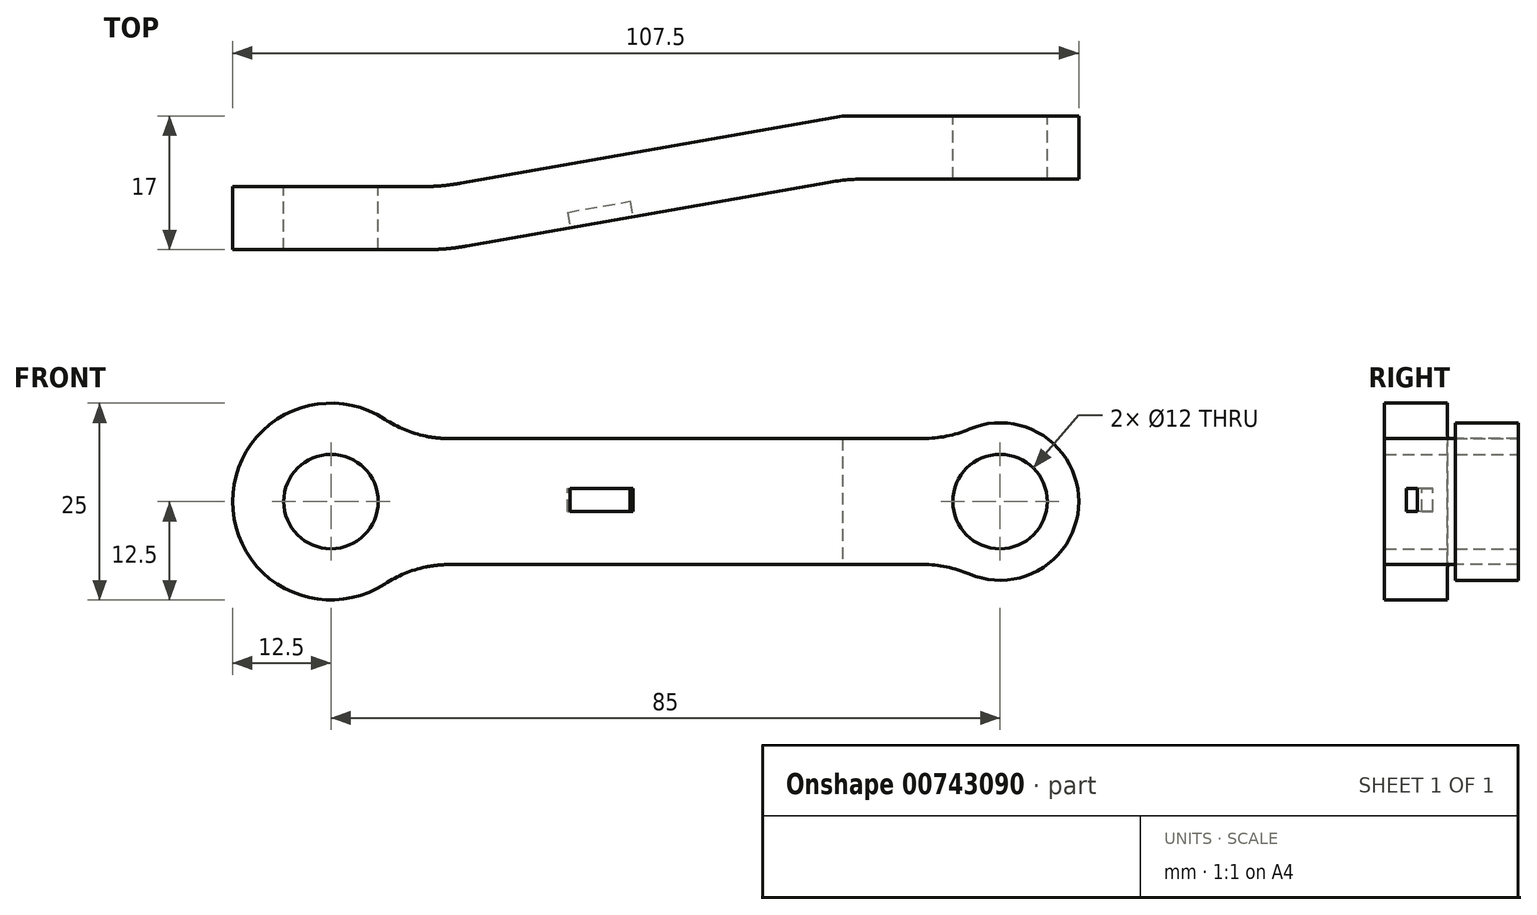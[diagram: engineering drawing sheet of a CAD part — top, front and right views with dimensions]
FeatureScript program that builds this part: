
annotation { "Feature Type Name" : "Feature", "Feature Type Description" : "" }
export const myFeature = defineFeature(function(context is Context, id is Id, definition is map)
    precondition{}
    {
        {
            var Q0;
            Q0=qCreatedBy(makeId("Front.planeOp"),FACE);
            var sketch = newSketch(context, id + "F0", { "sketchPlane" : qUnion([Q0])});
            skCircle(sketch, "E0", {"center": v(0, 0) * mm, "radius": 10 * mm});
            skCircle(sketch, "E1", {"center": v(-85, 0) * mm, "radius": 12.5 * mm});
            skCircle(sketch, "E2", {"center": v(-85, 0) * mm, "radius": 6 * mm});
            skCircle(sketch, "E3", {"center": v(0, 0) * mm, "radius": 6 * mm});
            skLineSegment(sketch, "E4", {"start": v(-85, 0) * mm, "end": v(0, 0) * mm, "construction": true});
            skLineSegment(sketch, "E5", {"start": v(-75.4, 8) * mm, "end": v(-6, 8) * mm});
            skLineSegment(sketch, "E6", {"start": v(-75.4, -8) * mm, "end": v(-6, -8) * mm});
            skSolve(sketch);
        }
        {
            var Q0;
            Q0=makeQuery(id+"F0.imprint","IMPRINT",FACE,{"disambiguationData":[TD([[makeQuery(id+"F0.imprint","IMPRINT",EDGE,{"derivedFrom":sQuery(id+"F0.wireOp",EDGE,"E2")}),-1.0]])]});
            var Q1;
            {var subQ0=sQuery(id+"F0.wireOp",EDGE,"E5");Q1=makeQuery(id+"F0.imprint","IMPRINT",FACE,{"disambiguationData":[TD([[makeQuery(id+"F0.imprint","IMPRINT",EDGE,{"derivedFrom":subQ0}),-1.0]])]});}
            var Q2;
            Q2=makeQuery(id+"F0.imprint","IMPRINT",FACE,{"disambiguationData":[TD([[makeQuery(id+"F0.imprint","IMPRINT",EDGE,{"derivedFrom":sQuery(id+"F0.wireOp",EDGE,"E3")}),-1.0]])]});
            extrude(context, id + "F1", {"entities" : qUnion([Q0, Q1, Q2]), "depth" : 25 * mm});
        }
        {
            var Q0;
            Q0=qCreatedBy(makeId("Top.planeOp"),FACE);
            var sketch = newSketch(context, id + "F2", { "sketchPlane" : qUnion([Q0])});
            skLineSegment(sketch, "E7", {"start": v(-110.22, -9) * mm, "end": v(-71.04, -9) * mm});
            skLineSegment(sketch, "E8", {"start": v(-71.04, -9) * mm, "end": v(-20, 0) * mm});
            skLineSegment(sketch, "E9", {"start": v(-20, 0) * mm, "end": v(29.22, 0) * mm});
            skLineSegment(sketch, "E10", {"start": v(29.22, 0) * mm, "end": v(29.22, -8) * mm});
            skLineSegment(sketch, "E11", {"start": v(29.22, -8) * mm, "end": v(-19.3, -8) * mm});
            skLineSegment(sketch, "E12", {"start": v(-19.3, -8) * mm, "end": v(-70.34, -17) * mm});
            skLineSegment(sketch, "E13", {"start": v(-70.34, -17) * mm, "end": v(-110.22, -17) * mm});
            skLineSegment(sketch, "E14", {"start": v(-110.22, -17) * mm, "end": v(-110.22, -9) * mm});
            skSolve(sketch);
        }
        {
            var Q0;
            Q0=makeQuery(id+"F2.imprint","IMPRINT",FACE,{"disambiguationData":[TD([[makeQuery(id+"F2.imprint","IMPRINT",EDGE,{"derivedFrom":sQuery(id+"F2.wireOp",EDGE,"E7")}),-1.0]])]});
            extrude(context, id + "F3", {"entities" : qUnion([Q0]), "operationType" : NewBodyOperationType.INTERSECT, "endBound" : BoundingType.SYMMETRIC, "depth" : 40 * mm});
        }
        {
            var Q0;
            Q0=makeQuery(id+"F3.boolean.opBoolean","COPY",EDGE,{"derivedFrom":makeQuery(id+"F3.opExtrude","SWEPT_EDGE",EDGE,{"disambiguationData":[OSD([sQuery(id+"F2.wireOp",EDGE,"E12"),sQuery(id+"F2.wireOp",EDGE,"E13")])]})});
            var Q1;
            Q1=makeQuery(id+"F3.boolean.opBoolean","COPY",EDGE,{"derivedFrom":makeQuery(id+"F3.opExtrude","SWEPT_EDGE",EDGE,{"disambiguationData":[OSD([sQuery(id+"F2.wireOp",EDGE,"E11"),sQuery(id+"F2.wireOp",EDGE,"E12")])]})});
            var Q2;
            Q2=makeQuery(id+"F3.boolean.opBoolean","COPY",EDGE,{"derivedFrom":makeQuery(id+"F3.opExtrude","SWEPT_EDGE",EDGE,{"disambiguationData":[OSD([sQuery(id+"F2.wireOp",EDGE,"E8"),sQuery(id+"F2.wireOp",EDGE,"E9")])]})});
            var Q3;
            Q3=makeQuery(id+"F3.boolean.opBoolean","COPY",EDGE,{"derivedFrom":makeQuery(id+"F3.opExtrude","SWEPT_EDGE",EDGE,{"disambiguationData":[OSD([sQuery(id+"F2.wireOp",EDGE,"E7"),sQuery(id+"F2.wireOp",EDGE,"E8")])]})});
            fillet(context, id + "F4", {"entities" : qUnion([Q0, Q1, Q2, Q3]), "radius" : 30 * mm, "tangentPropagation" : true, "allowEdgeOverflow" : false});
        }
        {
            var Q0;
            Q0=makeQuery(id+"F1.opExtrude","SWEPT_EDGE",EDGE,{"disambiguationData":[OSD([sQuery(id+"F0.wireOp",EDGE,"E1"),sQuery(id+"F0.wireOp",EDGE,"E5")])]});
            var Q1;
            Q1=makeQuery(id+"F1.opExtrude","SWEPT_EDGE",EDGE,{"disambiguationData":[OSD([sQuery(id+"F0.wireOp",EDGE,"E0"),sQuery(id+"F0.wireOp",EDGE,"E5")])]});
            var Q2;
            Q2=makeQuery(id+"F1.opExtrude","SWEPT_EDGE",EDGE,{"disambiguationData":[OSD([sQuery(id+"F0.wireOp",EDGE,"E1"),sQuery(id+"F0.wireOp",EDGE,"E6")])]});
            var Q3;
            Q3=makeQuery(id+"F1.opExtrude","SWEPT_EDGE",EDGE,{"disambiguationData":[OSD([sQuery(id+"F0.wireOp",EDGE,"E0"),sQuery(id+"F0.wireOp",EDGE,"E6")])]});
            fillet(context, id + "F5", {"entities" : qUnion([Q0, Q1, Q2, Q3]), "radius" : 15 * mm, "tangentPropagation" : true, "allowEdgeOverflow" : false});
        }
        {
            var Q0;
            Q0=makeQuery(id+"F3.boolean.opBoolean","COPY",FACE,{"derivedFrom":makeQuery(id+"F3.opExtrude","SWEPT_FACE",FACE,{"disambiguationData":[OSD([sQuery(id+"F2.wireOp",EDGE,"E12")])]})});
            var sketch = newSketch(context, id + "F6", { "sketchPlane" : qUnion([Q0])});
            skLineSegment(sketch, "E15.bottom", {"start": v(-56.24, -1.24) * mm, "end": v(-48.17, -1.24) * mm});
            skLineSegment(sketch, "E15.top", {"start": v(-56.24, 1.7) * mm, "end": v(-48.17, 1.7) * mm});
            skLineSegment(sketch, "E15.left", {"start": v(-56.24, -1.24) * mm, "end": v(-56.24, 1.7) * mm});
            skLineSegment(sketch, "E15.right", {"start": v(-48.17, -1.24) * mm, "end": v(-48.17, 1.7) * mm});
            skSolve(sketch);
        }
        {
            var Q0;
            Q0=makeQuery(id+"F6.imprint","IMPRINT",FACE,{"disambiguationData":[TD([[makeQuery(id+"F6.imprint","IMPRINT",EDGE,{"derivedFrom":sQuery(id+"F6.wireOp",EDGE,"E15.bottom")}),1.0]])]});
            extrude(context, id + "F7", {"entities" : qUnion([Q0]), "operationType" : NewBodyOperationType.REMOVE, "oppositeDirection" : true, "depth" : 2 * mm, "offsetDistance" : 25 * mm});
        }
    });
